# Revit family: 0043406
name_source: partatom
category: Lighting Devices
units: mm (PartAtom-declared; Revit-internal decimal feet)

## family parameters
Cut with Voids When Loaded = No
Host = Face
Maintain Annotation Orientation = No
OmniClass Number = 23.80.70.00
OmniClass Title = Lighting
Part Type = Normal
Room Calculation Point = No
Round Connector Dimension = Use Diameter
Shared = No

## types (1)
- START SURFACE IP54 MW 500-2000 830/840
    Apparent Load = 22 VA
    Assembly Code = D5020200
    AssetType = Fixed
    BodyHeight = 30 mm  [stored 0.0984252 ft]
    BodyRadius = 140 mm  [stored 0.459318 ft]
    BottomRadius = 130 mm  [stored 0.426509 ft]
    ClassificationName = Uniclass2015
    ClassificationValue = EF_70_80
    Cost = 0 $
    Default Elevation = 1219 mm
    Description = Ceiling / wall luminaire with integrated LED. Perfect solution for hallways, circulation spaces or foyers. Body Size diameter 300mm. Besa mounting box compatible, hole distance 51 & 78mm. DualTone functionality enables switch between 3000K and 4000K colour temperatures. With the help of DIP Switch multiple lumen outputs can be set up in 4 steps (4000K: 6W 500lm, 9.3W 1000lm, 13.5W 1500lm, 17.5W 2000lm). Efficacy up to 114lm/W. Supplied with integrated Microwave sensor for automatic on-off presence control. Non-dimmable. IK03, IP54. Low maintenance with lifespan 120,000 hours L70:B50.
    DiffuserRadius = 150 mm
    DocumentationLiterature = https://www.sylvania-lighting.com
    ElectricShockClassification = Class II
    Export Type to IFC As = IfcLightFixtureType
    IfcExportAs = IfcLightFixtureType
    IfcExportType = IfcLightFixtureType
    ImpactProtectionIndex = IK03
    IngressProtection = IP54
    InputNominalFrequency = 50/60Hz
    InputVoltage = 220-240 V
    Keynote = 16500
    Lamp = LED
    LampColourRenderingIndex = 80
    LampColourTemperature = 3000/4000K
    LampMacAdamStep = 6
    LampNominalLuminous = 2000 lm
    LampsType = LED
    LuminaireType = Ceiling / surface mounting
    LuminousEfficacy = 114 lm/W
    Manufacturer = Feilo Sylvania
    ManufacturerName = Feilo Sylvania
    Material = Polycarbonate
    Material_1_SYL = PC Polycarbonate_RAL 9003_Signal white
    Material_2_SYL = PMMA Acrylic_Opal_4000K
    Material_3_SYL = <By Category>
    Material_4_SYL = <By Category>
    Model = START SURFACE IP54 MW 500-2000 830/840
    ModelNumber = 0043406
    ModelReference = START SURFACE IP54 MW 500-2000 830/840
    Name = START SURFACE IP54 MW 500-2000 830/840
    NominalDepth = 300 mm
    NominalHeight = 94 mm  [stored 0.308399 ft]
    NominalLength = 300 mm
    PowerConsumption = 17.5 W
    PowerFactor = 0.8
    Type IFC Predefined Type = IfcLightFixtureType
    Type Image = <None>
    TypeName = START Surface IP54 - 300mm
    URL = http://www.sylvania-group.com
    Voltage = 230 V
    WarrantyDescription = http://www.sylvania-group.com
    WarrantyDurationParts = 5
    WarrantyDurationUnit = Years
    Weight = 0.6 kg

note: [stored X ft] marks values corroborated as IEEE doubles in the binary element streams (Revit-internal decimal feet)

## geometry (parser evidence)
native form markers: Sweep x21
no freeform markers — native parametric forms only
